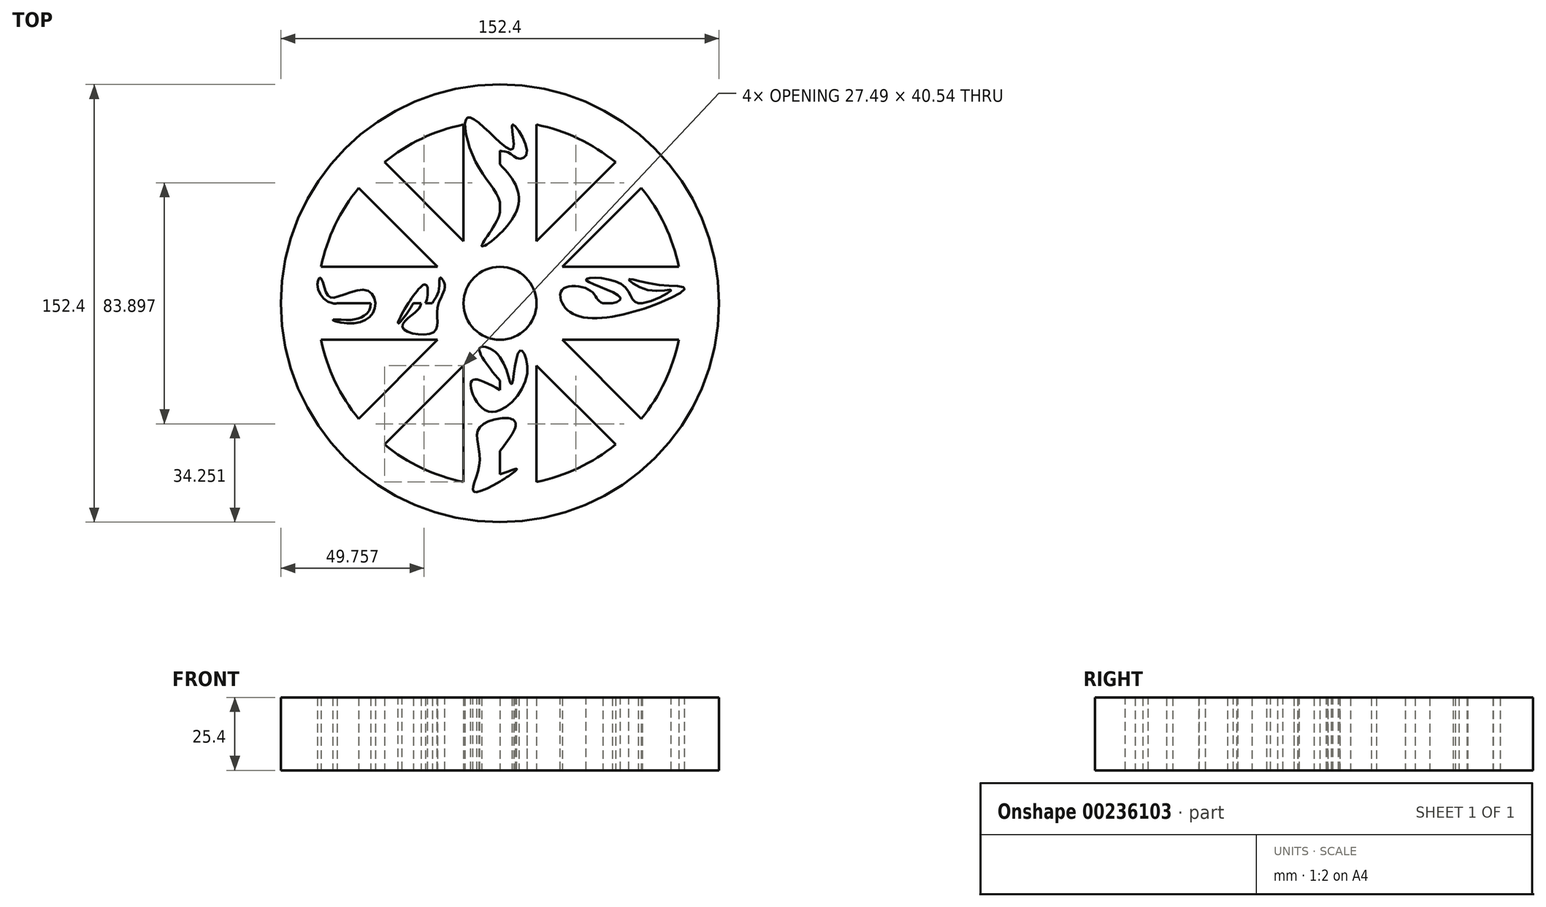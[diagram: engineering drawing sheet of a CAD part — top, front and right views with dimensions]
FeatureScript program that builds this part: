
annotation { "Feature Type Name" : "Feature", "Feature Type Description" : "" }
export const myFeature = defineFeature(function(context is Context, id is Id, definition is map)
    precondition{}
    {
        {
            var Q0;
            Q0=qCreatedBy(makeId("Top.planeOp"),FACE);
            var sketch = newSketch(context, id + "F0", { "sketchPlane" : qUnion([Q0])});
            skCircle(sketch, "E0", {"center": v(0, 0) * mm, "radius": 76.2 * mm});
            skArc(sketch, "E1", {"start": v(62.22, 12.7) * mm, "mid": v(44.9, 44.9) * mm, "end": v(12.7, 62.22) * mm});
            skCircle(sketch, "E2", {"center": v(0, 0) * mm, "radius": 12.7 * mm});
            skLineSegment(sketch, "E3", {"start": v(0, 0) * mm, "end": v(0, 63.5) * mm});
            skLineSegment(sketch, "E4.0", {"start": v(-12.7, 12.7) * mm, "end": v(-12.7, 62.22) * mm});
            skLineSegment(sketch, "E5.0", {"start": v(12.7, 12.7) * mm, "end": v(12.7, 62.22) * mm});
            skLineSegment(sketch, "E6", {"start": v(0, 0) * mm, "end": v(0, -63.5) * mm});
            skLineSegment(sketch, "E7", {"start": v(0, 0) * mm, "end": v(-63.5, 0) * mm});
            skLineSegment(sketch, "E8", {"start": v(0, 0) * mm, "end": v(63.5, 0) * mm});
            skLineSegment(sketch, "E9.0", {"start": v(12.7, 12.7) * mm, "end": v(62.22, 12.7) * mm});
            skLineSegment(sketch, "E10.0", {"start": v(12.7, -12.7) * mm, "end": v(62.22, -12.7) * mm});
            skLineSegment(sketch, "E11.0", {"start": v(-12.7, -12.7) * mm, "end": v(-12.7, -62.22) * mm});
            skLineSegment(sketch, "E12.0", {"start": v(12.7, -12.7) * mm, "end": v(12.7, -62.22) * mm});
            skLineSegment(sketch, "E13.0", {"start": v(-12.7, 12.7) * mm, "end": v(-62.22, 12.7) * mm});
            skLineSegment(sketch, "E14.0", {"start": v(-12.7, -12.7) * mm, "end": v(-62.22, -12.7) * mm});
            skLineSegment(sketch, "E15.trimOffspring", {"start": v(-12.7, 75.13) * mm, "end": v(-12.7, 76.2) * mm});
            skLineSegment(sketch, "E16.trimOffspring", {"start": v(12.7, 75.13) * mm, "end": v(12.7, 76.2) * mm});
            skLineSegment(sketch, "E17.trimOffspring", {"start": v(75.13, 12.7) * mm, "end": v(76.2, 12.7) * mm});
            skLineSegment(sketch, "E18.trimOffspring", {"start": v(75.13, -12.7) * mm, "end": v(76.2, -12.7) * mm});
            skLineSegment(sketch, "E19.trimOffspring", {"start": v(12.7, -75.13) * mm, "end": v(12.7, -76.2) * mm});
            skLineSegment(sketch, "E20.trimOffspring", {"start": v(-12.7, -75.13) * mm, "end": v(-12.7, -76.2) * mm});
            skArc(sketch, "E21.trimOffspring", {"start": v(12.7, -62.22) * mm, "mid": v(44.9, -44.9) * mm, "end": v(62.22, -12.7) * mm});
            skLineSegment(sketch, "E22.trimOffspring", {"start": v(-75.13, -12.7) * mm, "end": v(-76.2, -12.7) * mm});
            skLineSegment(sketch, "E23.trimOffspring", {"start": v(-75.13, 12.7) * mm, "end": v(-76.2, 12.7) * mm});
            skArc(sketch, "E24.trimOffspring", {"start": v(-62.22, -12.7) * mm, "mid": v(-44.9, -44.9) * mm, "end": v(-12.7, -62.22) * mm});
            skArc(sketch, "E25.trimOffspring", {"start": v(-12.7, 62.22) * mm, "mid": v(-44.9, 44.9) * mm, "end": v(-62.22, 12.7) * mm});
            skPoint(sketch, "E26.5.internal.snap0", {"position": v(-44.9, 44.9) * mm});
            skPoint(sketch, "E26.19.internal.snap0", {"position": v(-44.9, 44.9) * mm});
            skPoint(sketch, "E26.20.internal.snap0", {"position": v(-44.9, 44.9) * mm});
            skLineSegment(sketch, "E27.0", {"start": v(-40.41, 49.4) * mm, "end": v(-12.7, 21.68) * mm});
            skLineSegment(sketch, "E28.0", {"start": v(-49.4, 40.41) * mm, "end": v(-21.68, 12.7) * mm});
            skLineSegment(sketch, "E29.0", {"start": v(21.68, 12.7) * mm, "end": v(49.4, 40.41) * mm});
            skLineSegment(sketch, "E30.0", {"start": v(12.7, 21.68) * mm, "end": v(40.41, 49.4) * mm});
            skLineSegment(sketch, "E31.0", {"start": v(12.7, -21.68) * mm, "end": v(40.41, -49.4) * mm});
            skLineSegment(sketch, "E32.0", {"start": v(21.68, -12.7) * mm, "end": v(49.4, -40.41) * mm});
            skLineSegment(sketch, "E33.0", {"start": v(-21.68, -12.7) * mm, "end": v(-49.4, -40.41) * mm});
            skLineSegment(sketch, "E34.0", {"start": v(-12.7, -21.68) * mm, "end": v(-40.41, -49.4) * mm});
            skPoint(sketch, "E35.end.orphan", {"position": v(-44.9, -44.9) * mm});
            skPoint(sketch, "E36.end.orphan", {"position": v(44.9, -44.9) * mm});
            skPoint(sketch, "E37.end.orphan", {"position": v(44.9, 44.9) * mm});
            skSolve(sketch);
        }
        {
            var Q0;
            Q0=qCreatedBy(makeId("Top.planeOp"),FACE);
            var sketch = newSketch(context, id + "F1", { "sketchPlane" : qUnion([Q0])});
            skCircle(sketch, "E38", {"center": v(0, 0) * mm, "radius": 76.2 * mm});
            skArc(sketch, "E39", {"start": v(-12.7, 62.22) * mm, "mid": v(-44.9, 44.9) * mm, "end": v(-62.22, 12.7) * mm});
            skCircle(sketch, "E40", {"center": v(0, 0) * mm, "radius": 12.7 * mm});
            skLineSegment(sketch, "E41", {"start": v(0, 0) * mm, "end": v(0, 63.5) * mm});
            skLineSegment(sketch, "E42", {"start": v(0, 0) * mm, "end": v(63.5, 0) * mm});
            skLineSegment(sketch, "E43", {"start": v(0, 0) * mm, "end": v(0, -63.5) * mm});
            skLineSegment(sketch, "E44", {"start": v(0, 0) * mm, "end": v(-63.5, 0) * mm});
            skLineSegment(sketch, "E45.0", {"start": v(12.7, 12.7) * mm, "end": v(12.7, 62.22) * mm});
            skLineSegment(sketch, "E46.0", {"start": v(-12.7, 12.7) * mm, "end": v(-12.7, 62.22) * mm});
            skLineSegment(sketch, "E47.0", {"start": v(12.7, 12.7) * mm, "end": v(62.22, 12.7) * mm});
            skLineSegment(sketch, "E48.0", {"start": v(12.7, -12.7) * mm, "end": v(62.22, -12.7) * mm});
            skLineSegment(sketch, "E49.0", {"start": v(12.7, -12.7) * mm, "end": v(12.7, -62.22) * mm});
            skLineSegment(sketch, "E50.0", {"start": v(-12.7, -12.7) * mm, "end": v(-12.7, -62.22) * mm});
            skLineSegment(sketch, "E51.0", {"start": v(-12.7, 12.7) * mm, "end": v(-62.22, 12.7) * mm});
            skLineSegment(sketch, "E52.0", {"start": v(-12.7, -12.7) * mm, "end": v(-62.22, -12.7) * mm});
            skLineSegment(sketch, "E53.trimOffspring", {"start": v(-12.7, 75.13) * mm, "end": v(-12.7, 76.2) * mm});
            skLineSegment(sketch, "E54.trimOffspring", {"start": v(12.7, 75.13) * mm, "end": v(12.7, 76.2) * mm});
            skLineSegment(sketch, "E55.trimOffspring", {"start": v(-75.13, 12.7) * mm, "end": v(-76.2, 12.7) * mm});
            skArc(sketch, "E56.trimOffspring", {"start": v(-62.22, -12.7) * mm, "mid": v(-44.9, -44.9) * mm, "end": v(-12.7, -62.22) * mm});
            skLineSegment(sketch, "E57.trimOffspring", {"start": v(-75.13, -12.7) * mm, "end": v(-76.2, -12.7) * mm});
            skLineSegment(sketch, "E58.trimOffspring", {"start": v(75.13, -12.7) * mm, "end": v(76.2, -12.7) * mm});
            skLineSegment(sketch, "E59.trimOffspring", {"start": v(75.13, 12.7) * mm, "end": v(76.2, 12.7) * mm});
            skArc(sketch, "E60.trimOffspring", {"start": v(62.22, 12.7) * mm, "mid": v(44.9, 44.9) * mm, "end": v(12.7, 62.22) * mm});
            skLineSegment(sketch, "E61.trimOffspring", {"start": v(-12.7, -75.13) * mm, "end": v(-12.7, -76.2) * mm});
            skLineSegment(sketch, "E62.trimOffspring", {"start": v(12.7, -75.13) * mm, "end": v(12.7, -76.2) * mm});
            skArc(sketch, "E63.trimOffspring", {"start": v(12.7, -62.22) * mm, "mid": v(44.9, -44.9) * mm, "end": v(62.22, -12.7) * mm});
            skFitSpline(sketch, "E64", {"points": [v(-62.5, 8.91) * mm, v(-60.34, 3.43) * mm, v(-57.4, 2.06) * mm, v(-46.43, 4.6) * mm, v(-43.5, -1.66) * mm, v(-50.54, -6.95) * mm, v(-58.18, -5.78) * mm, v(-53.09, -5.78) * mm, v(-48.58, -5) * mm, v(-45.45, -2.45) * mm, v(-45.65, 1.66) * mm, v(-50.74, 2.25) * mm, v(-58.18, 0) * mm, v(-63.5, 5.78) * mm, v(-62.5, 8.91) * mm]});
            skPoint(sketch, "E65.17.internal.snap0", {"position": v(-31.75, 0) * mm});
            skFitSpline(sketch, "E65", {"points": [v(-30.37, -5.58) * mm, v(-25.86, 0) * mm, v(-26.26, 6.56) * mm, v(-35.46, -6.76) * mm, v(-31.15, -1.66) * mm, v(-27.43, 4.21) * mm, v(-27.43, 0) * mm, v(-29.78, -3.43) * mm, v(-33.9, -8.52) * mm, v(-23.12, -10.09) * mm, v(-21.75, -1.66) * mm, v(-19.2, 6.17) * mm, v(-20.77, 8.91) * mm, v(-21.36, 4.21) * mm, v(-24.1, -1.66) * mm, v(-23.71, -6.56) * mm, v(-26.65, -8.13) * mm, v(-31.75, -8.13) * mm, v(-30.37, -5.58) * mm]});
            skPoint(sketch, "E66.8.internal.snap0", {"position": v(0, -31.75) * mm});
            skFitSpline(sketch, "E66", {"points": [v(-10.2, -28.3) * mm, v(-3.73, -37.7) * mm, v(9.4, -24.97) * mm, v(6.84, -16.55) * mm, v(4.1, -28.1) * mm, v(0, -18.7) * mm, v(-7.06, -15.57) * mm, v(0, -26.93) * mm, v(3.32, -31.75) * mm, v(-7.85, -26.54) * mm, v(-10.2, -28.3) * mm]});
            skFitSpline(sketch, "E67", {"points": [v(-6.28, -60.82) * mm, v(5.47, -41.82) * mm, v(-6.67, -42.8) * mm, v(-7.06, -55.53) * mm, v(-8.63, -65.71) * mm, v(5.87, -57.68) * mm, v(-6.28, -60.82) * mm]});
            skPoint(sketch, "E68.12.internal.snap0", {"position": v(31.75, 0) * mm});
            skFitSpline(sketch, "E68", {"points": [v(21.73, 4.8) * mm, v(27.8, -4.6) * mm, v(64.23, 5) * mm, v(54.24, 6.56) * mm, v(44.84, 8.32) * mm, v(52.48, 4.4) * mm, v(59.53, 4.6) * mm, v(48.17, 0) * mm, v(42.5, 6.56) * mm, v(29.96, 8.13) * mm, v(41.9, 1.86) * mm, v(35.83, 0) * mm, v(31.75, 4.21) * mm, v(21.73, 4.8) * mm]});
            skFitSpline(sketch, "E69", {"points": [v(-8.82, 57.1) * mm, v(6.65, 36.33) * mm, v(-6.28, 19.88) * mm, v(0, 31.75) * mm, v(-8.04, 48.48) * mm, v(-10.59, 64.73) * mm, v(4.3, 53.57) * mm, v(4.3, 62.22) * mm, v(9.4, 52.59) * mm, v(6.26, 50.43) * mm, v(2.34, 52.79) * mm, v(0, 53.18) * mm, v(0, 54.55) * mm, v(-3.14, 55.92) * mm, v(-4.9, 58.66) * mm, v(-5.7, 58.66) * mm, v(-6.67, 59.64) * mm, v(-7.85, 58.86) * mm, v(-8.82, 57.1) * mm]});
            skSolve(sketch);
        }
        {
            var Q0;
            Q0 = qSketchRegion(id + "F1", true);
            extrude(context, id + "F2", {"entities" : qUnion([Q0]), "depth" : 25.4 * mm});
        }
        {
            var Q0;
            {var subQ1=sQuery(id+"F0.wireOp",EDGE,"E4.0");var subQ5=sQuery(id+"F0.wireOp",EDGE,"E13.0");var subQ6=makeQuery(id+"F0.imprint","INTERSECT",VERTEX,{"derivedFrom":[subQ1,subQ5]});Q0=makeQuery(id+"F0.imprint","IMPRINT",FACE,{"disambiguationData":[TD([[makeQuery(id+"F0.imprint","IMPRINT",EDGE,{"disambiguationData":[TD([[subQ6,-1.0]])],"derivedFrom":subQ1}),1.0]])]});}
            extrude(context, id + "F3", {"entities" : qUnion([Q0]), "operationType" : NewBodyOperationType.ADD, "depth" : 25.4 * mm});
        }
        {
            var Q0;
            {var subQ1=sQuery(id+"F0.wireOp",EDGE,"E4.0");var subQ5=sQuery(id+"F0.wireOp",EDGE,"E13.0");var subQ6=makeQuery(id+"F0.imprint","INTERSECT",VERTEX,{"derivedFrom":[subQ1,subQ5]});Q0=makeQuery(id+"F0.imprint","IMPRINT",FACE,{"disambiguationData":[TD([[makeQuery(id+"F0.imprint","IMPRINT",EDGE,{"disambiguationData":[TD([[subQ6,-1.0]])],"derivedFrom":subQ1}),1.0]])]});}
            var Q1;
            {var subQ0=sQuery(id+"F0.wireOp",EDGE,"E29.0");var subQ3=sQuery(id+"F0.wireOp",EDGE,"E1");var subQ4=makeQuery(id+"F0.imprint","INTERSECT",VERTEX,{"derivedFrom":[subQ3,subQ0]});Q1=makeQuery(id+"F0.imprint","IMPRINT",FACE,{"disambiguationData":[TD([[makeQuery(id+"F0.imprint","IMPRINT",EDGE,{"disambiguationData":[TD([[subQ4,-1.0]])],"derivedFrom":subQ3}),1.0]])]});}
            var Q2;
            {var subQ1=sQuery(id+"F0.wireOp",EDGE,"E12.0");var subQ7=sQuery(id+"F0.wireOp",EDGE,"E10.0");var subQ8=makeQuery(id+"F0.imprint","INTERSECT",VERTEX,{"derivedFrom":[subQ7,subQ1]});Q2=makeQuery(id+"F0.imprint","IMPRINT",FACE,{"disambiguationData":[TD([[makeQuery(id+"F0.imprint","IMPRINT",EDGE,{"disambiguationData":[TD([[subQ8,-1.0]])],"derivedFrom":subQ7}),-1.0]])]});}
            var Q3;
            {var subQ1=sQuery(id+"F0.wireOp",EDGE,"E14.0");var subQ7=sQuery(id+"F0.wireOp",EDGE,"E11.0");var subQ8=makeQuery(id+"F0.imprint","INTERSECT",VERTEX,{"derivedFrom":[subQ7,subQ1]});Q3=makeQuery(id+"F0.imprint","IMPRINT",FACE,{"disambiguationData":[TD([[makeQuery(id+"F0.imprint","IMPRINT",EDGE,{"disambiguationData":[TD([[subQ8,-1.0]])],"derivedFrom":subQ7}),-1.0]])]});}
            extrude(context, id + "F4", {"entities" : qUnion([Q0, Q1, Q2, Q3]), "operationType" : NewBodyOperationType.ADD, "depth" : 25.4 * mm});
        }
    });
